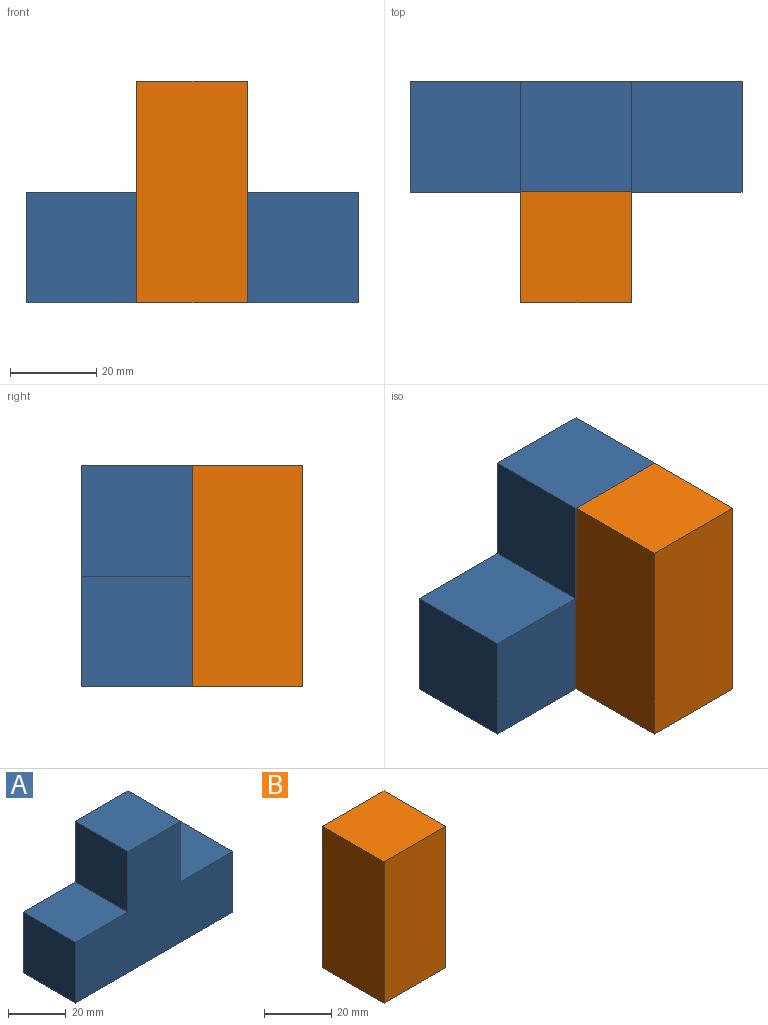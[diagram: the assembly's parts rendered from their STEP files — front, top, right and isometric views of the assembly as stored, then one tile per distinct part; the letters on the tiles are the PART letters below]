
ASSEMBLY  parts=2 mates=1
PART A: 10 faces, bbox 77x25.7x51.3 mm
  f0: plane 25.65x25.65mm, normal (-1,0,0), area 658.1mm2, adj f1,f7,f8,f9
  f1: plane 76.96x25.65mm, normal (0,0,-1), area 1974.4mm2, adj f0,f2,f8,f9
  f2: plane 25.65x25.65mm, normal (1,0,0), area 658.1mm2, adj f1,f3,f8,f9
  f3: plane 25.65x25.65mm, normal (0,0,1), area 658.1mm2, adj f2,f4,f8,f9
  f4: plane 25.65x25.65mm, normal (1,0,0), area 658.1mm2, adj f3,f5,f8,f9
  f5: plane 25.65x25.65mm, normal (0,0,1), area 658.1mm2, adj f4,f6,f8,f9
  f6: plane 25.65x25.65mm, normal (-1,0,0), area 658.1mm2, adj f5,f7,f8,f9
  f7: plane 25.65x25.65mm, normal (0,0,1), area 658.1mm2, adj f0,f6,f8,f9
  f8: plane 76.96x51.31mm, normal (0,-1,0), area 2632.5mm2, adj f0,f1,f2,f3,f4,f5,f6,f7
  f9: plane 76.96x51.31mm, normal (0,1,0), area 2632.5mm2, adj f0,f1,f2,f3,f4,f5,f6,f7
PART B: 6 faces, bbox 25.7x25.7x51.3 mm
  f0: plane 51.31x25.65mm, normal (-1,0,0), area 1316.3mm2, adj f1,f3,f4,f5
  f1: plane 25.65x25.65mm, normal (0,0,-1), area 658.1mm2, adj f0,f2,f4,f5
  f2: plane 51.31x25.65mm, normal (1,0,0), area 1316.3mm2, adj f1,f3,f4,f5
  f3: plane 25.65x25.65mm, normal (0,0,1), area 658.1mm2, adj f0,f2,f4,f5
  f4: plane 51.31x25.65mm, normal (0,-1,0), area 1316.3mm2, adj f0,f1,f2,f3
  f5: plane 51.31x25.65mm, normal (0,1,0), area 1316.3mm2, adj f0,f1,f2,f3
PLACE A t=(29.33,-3.76,18.16)mm
PLACE B t=(52.75,-29.42,21.22)mm
MATE fastened B.f5 <-> A.f8  axis (0,1,0) through (10.2,-16.59,28.34)mm
